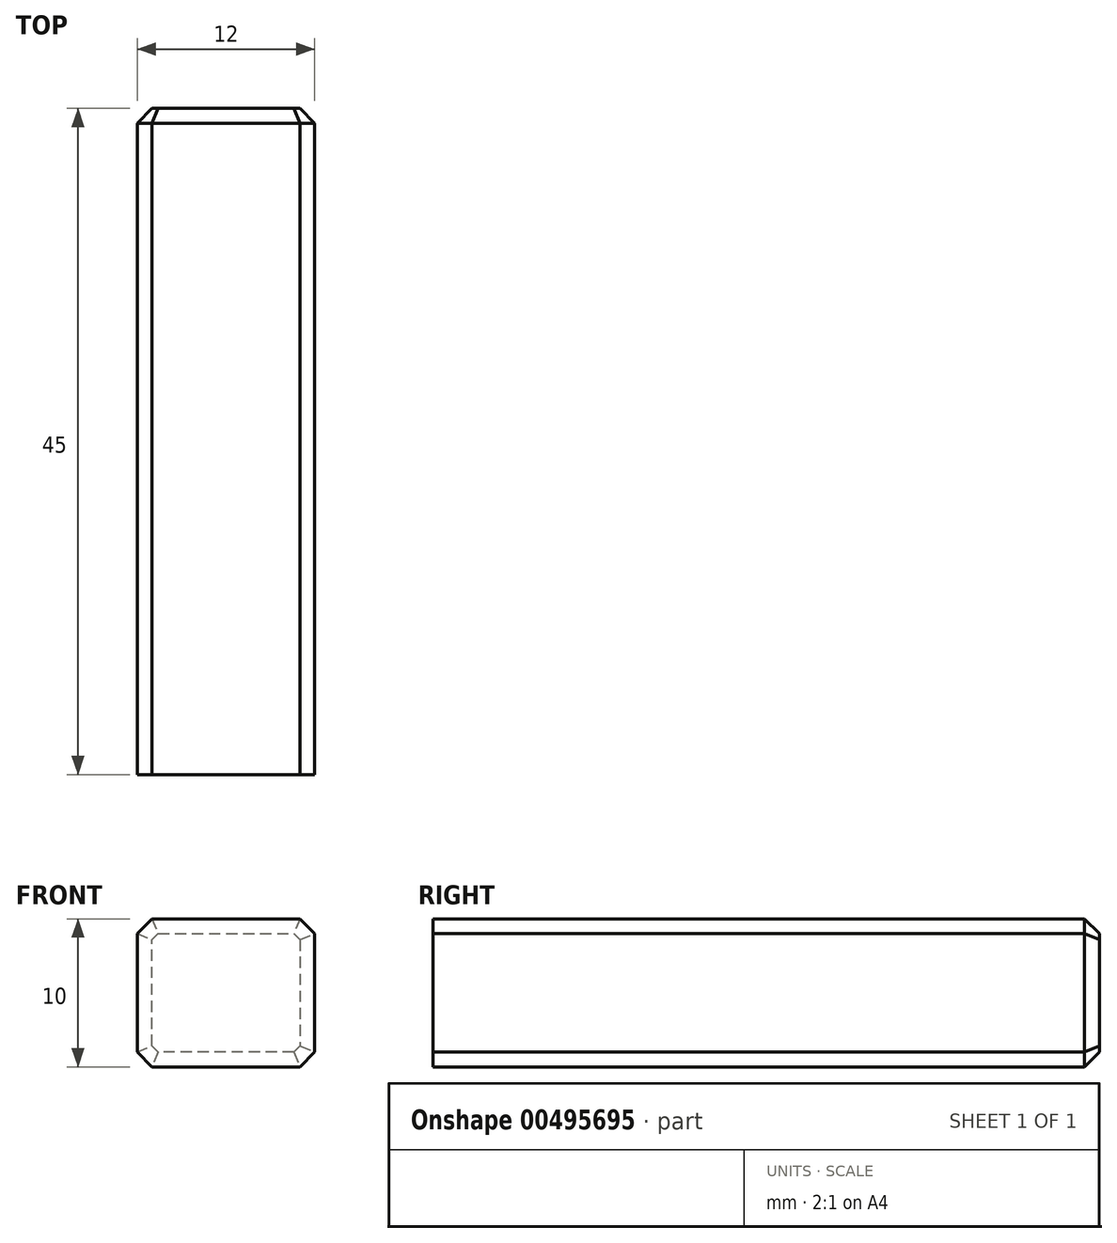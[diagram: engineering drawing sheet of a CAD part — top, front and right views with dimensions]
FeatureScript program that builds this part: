
annotation { "Feature Type Name" : "Feature", "Feature Type Description" : "" }
export const myFeature = defineFeature(function(context is Context, id is Id, definition is map)
    precondition{}
    {
        {
            var Q0;
            Q0=qCreatedBy(makeId("Front.planeOp"),FACE);
            var sketch = newSketch(context, id + "F0", { "sketchPlane" : qUnion([Q0])});
            skLineSegment(sketch, "E0.bottom", {"start": v(6, -5) * mm, "end": v(-6, -5) * mm});
            skLineSegment(sketch, "E0.top", {"start": v(6, 5) * mm, "end": v(-6, 5) * mm});
            skLineSegment(sketch, "E0.left", {"start": v(6, -5) * mm, "end": v(6, 5) * mm});
            skLineSegment(sketch, "E0.right", {"start": v(-6, -5) * mm, "end": v(-6, 5) * mm});
            skPoint(sketch, "E0.middle", {"position": v(0, 0) * mm});
            skSolve(sketch);
        }
        {
            var Q0;
            Q0=makeQuery(id+"F0.imprint","IMPRINT",FACE,{"disambiguationData":[TD([[makeQuery(id+"F0.imprint","IMPRINT",EDGE,{"derivedFrom":sQuery(id+"F0.wireOp",EDGE,"E0.bottom")}),-1.0]])]});
            extrude(context, id + "F1", {"entities" : qUnion([Q0]), "depth" : 45 * mm});
        }
        {
            var Q0;
            Q0=makeQuery(id+"F1.opExtrude","SWEPT_EDGE",EDGE,{"disambiguationData":[OSD([sQuery(id+"F0.wireOp",EDGE,"E0.top"),sQuery(id+"F0.wireOp",EDGE,"E0.left")])]});
            var Q1;
            Q1=makeQuery(id+"F1.opExtrude","SWEPT_EDGE",EDGE,{"disambiguationData":[OSD([sQuery(id+"F0.wireOp",EDGE,"E0.top"),sQuery(id+"F0.wireOp",EDGE,"E0.right")])]});
            var Q2;
            Q2=makeQuery(id+"F1.opExtrude","SWEPT_EDGE",EDGE,{"disambiguationData":[OSD([sQuery(id+"F0.wireOp",EDGE,"E0.bottom"),sQuery(id+"F0.wireOp",EDGE,"E0.left")])]});
            var Q3;
            Q3=makeQuery(id+"F1.opExtrude","SWEPT_EDGE",EDGE,{"disambiguationData":[OSD([sQuery(id+"F0.wireOp",EDGE,"E0.bottom"),sQuery(id+"F0.wireOp",EDGE,"E0.right")])]});
            chamfer(context, id + "F2", {"entities" : qUnion([Q0, Q1, Q2, Q3]), "width" : 1 * mm, "tangentPropagation" : true});
        }
        {
            var Q0;
            Q0=makeQuery(id+"F1.opExtrude","CAP_FACE",FACE,{"disambiguationData":[OSD([sQuery(id+"F0.wireOp",EDGE,"E0.bottom"),sQuery(id+"F0.wireOp",EDGE,"E0.top"),sQuery(id+"F0.wireOp",EDGE,"E0.left"),sQuery(id+"F0.wireOp",EDGE,"E0.right")])],"isStart":true});
            chamfer(context, id + "F3", {"entities" : qUnion([Q0]), "width" : 1 * mm, "tangentPropagation" : true});
        }
    });
